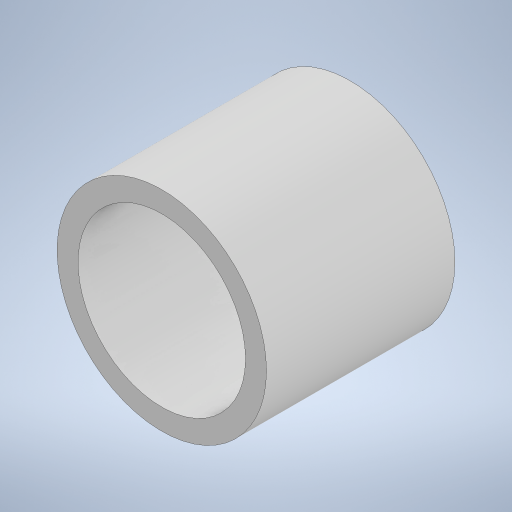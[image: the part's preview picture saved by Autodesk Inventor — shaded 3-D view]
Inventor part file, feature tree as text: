
AUTODESK INVENTOR PART (.ipt)
format: ipt  version: 2024 (Build 280153000, 153)  size: 200,192 bytes
history: native  units: in
note: dims shown in document units (in); Inventor stores cm internally (conversion verified against a paired STEP export)
features: extrude x2, sketch x1
ambient origin geometry x8: Origin, YZ Plane, XZ Plane, XY Plane, X Axis, Y Axis, Z Axis, Center Point
bodies: Solid1 (feature_tree)
feature tree (3):
  sketch  "Sketch1"  dims[d0=0.1575in d1=0.1969in d2=0.0394in d3=0.0in d4=0.1772in d5=0.0in]
  extrude  "Extrusion1"  Depth=0.1772in
  extrude  "Extrusion2"  Depth=0.0394in TaperAngle=0.0deg
